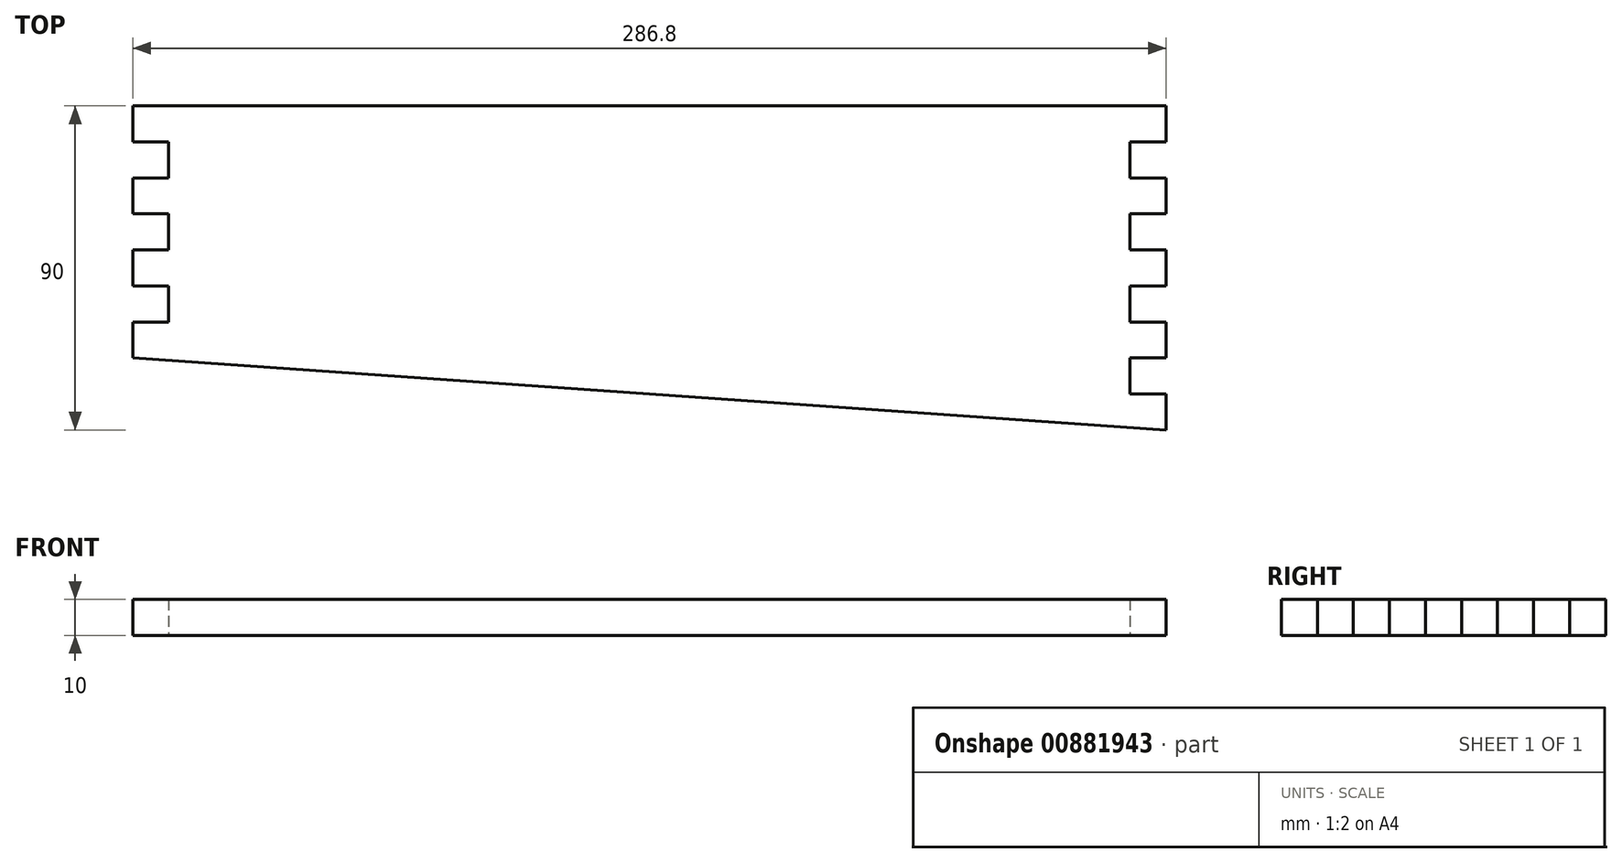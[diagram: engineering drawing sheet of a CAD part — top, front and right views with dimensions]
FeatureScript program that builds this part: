
annotation { "Feature Type Name" : "Feature", "Feature Type Description" : "" }
export const myFeature = defineFeature(function(context is Context, id is Id, definition is map)
    precondition{}
    {
        {
            var Q0;
            Q0=qCreatedBy(makeId("Top.planeOp"),FACE);
            var sketch = newSketch(context, id + "F0", { "sketchPlane" : qUnion([Q0])});
            skLineSegment(sketch, "E0.bottom", {"start": v(-145.63, 36.94) * mm, "end": v(141.17, 36.94) * mm});
            skLineSegment(sketch, "E0.top", {"start": v(-145.63, -33.06) * mm, "end": v(141.17, -33.06) * mm});
            skLineSegment(sketch, "E0.left", {"start": v(-145.63, 36.94) * mm, "end": v(-145.63, -33.06) * mm});
            skLineSegment(sketch, "E0.right", {"start": v(141.17, 36.94) * mm, "end": v(141.17, -33.06) * mm});
            skLineSegment(sketch, "E1.bottom", {"start": v(-145.63, 36.94) * mm, "end": v(-135.63, 36.94) * mm});
            skLineSegment(sketch, "E1.top", {"start": v(-145.63, -33.06) * mm, "end": v(-135.63, -33.06) * mm});
            skLineSegment(sketch, "E1.right", {"start": v(-135.63, 36.94) * mm, "end": v(-135.63, -33.06) * mm});
            skLineSegment(sketch, "E2.bottom", {"start": v(141.17, 36.94) * mm, "end": v(131.17, 36.94) * mm});
            skLineSegment(sketch, "E2.top", {"start": v(141.17, -33.06) * mm, "end": v(131.17, -33.06) * mm});
            skLineSegment(sketch, "E2.right", {"start": v(131.17, 36.94) * mm, "end": v(131.17, -33.06) * mm});
            skLineSegment(sketch, "E3.left", {"start": v(-145.63, 36.94) * mm, "end": v(-145.63, 26.94) * mm});
            skLineSegment(sketch, "E4.bottom", {"start": v(131.17, 36.94) * mm, "end": v(141.17, 36.94) * mm});
            skLineSegment(sketch, "E4.top", {"start": v(131.17, 26.94) * mm, "end": v(141.17, 26.94) * mm});
            skLineSegment(sketch, "E4.left", {"start": v(131.17, 36.94) * mm, "end": v(131.17, 26.94) * mm});
            skLineSegment(sketch, "E4.right", {"start": v(141.17, 36.94) * mm, "end": v(141.17, 26.94) * mm});
            skLineSegment(sketch, "E5.MirrorCS", {"start": v(141.17, 16.94) * mm, "end": v(131.17, 16.94) * mm});
            skLineSegment(sketch, "E6.MirrorCS", {"start": v(131.17, 6.94) * mm, "end": v(141.17, 6.94) * mm});
            skLineSegment(sketch, "E7.MirrorCS", {"start": v(141.17, -3.06) * mm, "end": v(131.17, -3.06) * mm});
            skLineSegment(sketch, "E8.MirrorCS", {"start": v(131.17, -13.06) * mm, "end": v(141.17, -13.06) * mm});
            skLineSegment(sketch, "E9.MirrorCS", {"start": v(141.17, -23.06) * mm, "end": v(131.17, -23.06) * mm});
            skLineSegment(sketch, "E10.MirrorCS", {"start": v(131.17, -33.06) * mm, "end": v(141.17, -33.06) * mm});
            skLineSegment(sketch, "E11.top", {"start": v(-145.63, 26.94) * mm, "end": v(-135.63, 26.94) * mm});
            skLineSegment(sketch, "E11.right", {"start": v(-135.63, 36.94) * mm, "end": v(-135.63, 26.94) * mm});
            skLineSegment(sketch, "E12.MirrorCS", {"start": v(-145.63, 16.94) * mm, "end": v(-135.63, 16.94) * mm});
            skLineSegment(sketch, "E13.MirrorCS", {"start": v(-145.63, 6.94) * mm, "end": v(-135.63, 6.94) * mm});
            skLineSegment(sketch, "E14.MirrorCS", {"start": v(-145.63, -3.06) * mm, "end": v(-135.63, -3.06) * mm});
            skLineSegment(sketch, "E15.MirrorCS", {"start": v(-145.63, -13.06) * mm, "end": v(-135.63, -13.06) * mm});
            skLineSegment(sketch, "E16.MirrorCS", {"start": v(-145.63, -23.06) * mm, "end": v(-135.63, -23.06) * mm});
            skLineSegment(sketch, "E17", {"start": v(141.17, -33.06) * mm, "end": v(141.17, -53.06) * mm});
            skLineSegment(sketch, "E18", {"start": v(141.17, -53.06) * mm, "end": v(-145.63, -33.06) * mm});
            skLineSegment(sketch, "E19", {"start": v(131.17, -33.06) * mm, "end": v(131.17, -52.36) * mm});
            skLineSegment(sketch, "E20.MirrorCS", {"start": v(141.17, -43.06) * mm, "end": v(131.17, -43.06) * mm});
            skLineSegment(sketch, "E21.bottom", {"start": v(131.17, -43.06) * mm, "end": v(141.17, -43.06) * mm, "construction": true});
            skLineSegment(sketch, "E21.top", {"start": v(131.17, -53.06) * mm, "end": v(141.17, -53.06) * mm, "construction": true});
            skLineSegment(sketch, "E21.left", {"start": v(131.17, -43.06) * mm, "end": v(131.17, -53.06) * mm, "construction": true});
            skLineSegment(sketch, "E21.right", {"start": v(141.17, -43.06) * mm, "end": v(141.17, -53.06) * mm, "construction": true});
            skSolve(sketch);
        }
        {
            var Q0;
            {var subQ0=sQuery(id+"F0.wireOp",EDGE,"E1.right");var subQ1=sQuery(id+"F0.wireOp",EDGE,"E0.bottom");var subQ2=makeQuery(id+"F0.imprint","INTERSECT",VERTEX,{"derivedFrom":[subQ1,subQ0]});Q0=makeQuery(id+"F0.imprint","IMPRINT",FACE,{"disambiguationData":[TD([[makeQuery(id+"F0.imprint","IMPRINT",EDGE,{"disambiguationData":[TD([[subQ2,-1.0]])],"derivedFrom":subQ1}),-1.0]])]});}
            var Q1;
            {var subQ5=sQuery(id+"F0.wireOp",EDGE,"E11.top");Q1=makeQuery(id+"F0.imprint","IMPRINT",FACE,{"disambiguationData":[TD([[makeQuery(id+"F0.imprint","IMPRINT",EDGE,{"derivedFrom":subQ5}),1.0]])]});}
            var Q2;
            {var subQ0=sQuery(id+"F0.wireOp",EDGE,"E12.MirrorCS");Q2=makeQuery(id+"F0.imprint","IMPRINT",FACE,{"disambiguationData":[TD([[makeQuery(id+"F0.imprint","IMPRINT",EDGE,{"derivedFrom":subQ0}),-1.0]])]});}
            var Q3;
            {var subQ0=sQuery(id+"F0.wireOp",EDGE,"E14.MirrorCS");Q3=makeQuery(id+"F0.imprint","IMPRINT",FACE,{"disambiguationData":[TD([[makeQuery(id+"F0.imprint","IMPRINT",EDGE,{"derivedFrom":subQ0}),-1.0]])]});}
            var Q4;
            {var subQ2=sQuery(id+"F0.wireOp",EDGE,"E16.MirrorCS");Q4=makeQuery(id+"F0.imprint","IMPRINT",FACE,{"disambiguationData":[TD([[makeQuery(id+"F0.imprint","IMPRINT",EDGE,{"derivedFrom":subQ2}),-1.0]])]});}
            var Q5;
            {var subQ5=sQuery(id+"F0.wireOp",EDGE,"f68d17bd-8033-4fb8-93ba-191072b4510d0.MirrorCS");Q5=makeQuery(id+"F0.imprint","IMPRINT",FACE,{"disambiguationData":[TD([[makeQuery(id+"F0.imprint","IMPRINT",EDGE,{"derivedFrom":subQ5}),-1.0]])]});}
            var Q6;
            {var subQ5=sQuery(id+"F0.wireOp",EDGE,"E4.top");Q6=makeQuery(id+"F0.imprint","IMPRINT",FACE,{"disambiguationData":[TD([[makeQuery(id+"F0.imprint","IMPRINT",EDGE,{"derivedFrom":subQ5}),1.0]])]});}
            var Q7;
            {var subQ0=sQuery(id+"F0.wireOp",EDGE,"E5.MirrorCS");Q7=makeQuery(id+"F0.imprint","IMPRINT",FACE,{"disambiguationData":[TD([[makeQuery(id+"F0.imprint","IMPRINT",EDGE,{"derivedFrom":subQ0}),1.0]])]});}
            var Q8;
            {var subQ0=sQuery(id+"F0.wireOp",EDGE,"E7.MirrorCS");Q8=makeQuery(id+"F0.imprint","IMPRINT",FACE,{"disambiguationData":[TD([[makeQuery(id+"F0.imprint","IMPRINT",EDGE,{"derivedFrom":subQ0}),1.0]])]});}
            var Q9;
            {var subQ0=sQuery(id+"F0.wireOp",EDGE,"E9.MirrorCS");Q9=makeQuery(id+"F0.imprint","IMPRINT",FACE,{"disambiguationData":[TD([[makeQuery(id+"F0.imprint","IMPRINT",EDGE,{"derivedFrom":subQ0}),1.0]])]});}
            var Q10;
            {var subQ5=sQuery(id+"F0.wireOp",EDGE,"e518cc57-b2af-43e8-af13-6bb7c84993f30.MirrorCS");Q10=makeQuery(id+"F0.imprint","IMPRINT",FACE,{"disambiguationData":[TD([[makeQuery(id+"F0.imprint","IMPRINT",EDGE,{"derivedFrom":subQ5}),1.0]])]});}
            var Q11;
            {var subQ0=sQuery(id+"F0.wireOp",EDGE,"E19");var subQ5=sQuery(id+"F0.wireOp",EDGE,"E18");var subQ7=makeQuery(id+"F0.imprint","INTERSECT",VERTEX,{"derivedFrom":[subQ5,subQ0]});Q11=makeQuery(id+"F0.imprint","IMPRINT",FACE,{"disambiguationData":[TD([[makeQuery(id+"F0.imprint","IMPRINT",EDGE,{"disambiguationData":[TD([[subQ7,1.0]])],"derivedFrom":subQ0}),-1.0]])]});}
            var Q12;
            {var subQ0=sQuery(id+"F0.wireOp",EDGE,"E20.MirrorCS");Q12=makeQuery(id+"F0.imprint","IMPRINT",FACE,{"disambiguationData":[TD([[makeQuery(id+"F0.imprint","IMPRINT",EDGE,{"derivedFrom":subQ0}),1.0]])]});}
            extrude(context, id + "F1", {"entities" : qUnion([Q0, Q1, Q2, Q3, Q4, Q5, Q6, Q7, Q8, Q9, Q10, Q11, Q12]), "depth" : 10 * mm, "offsetDistance" : 25 * mm});
        }
    });
